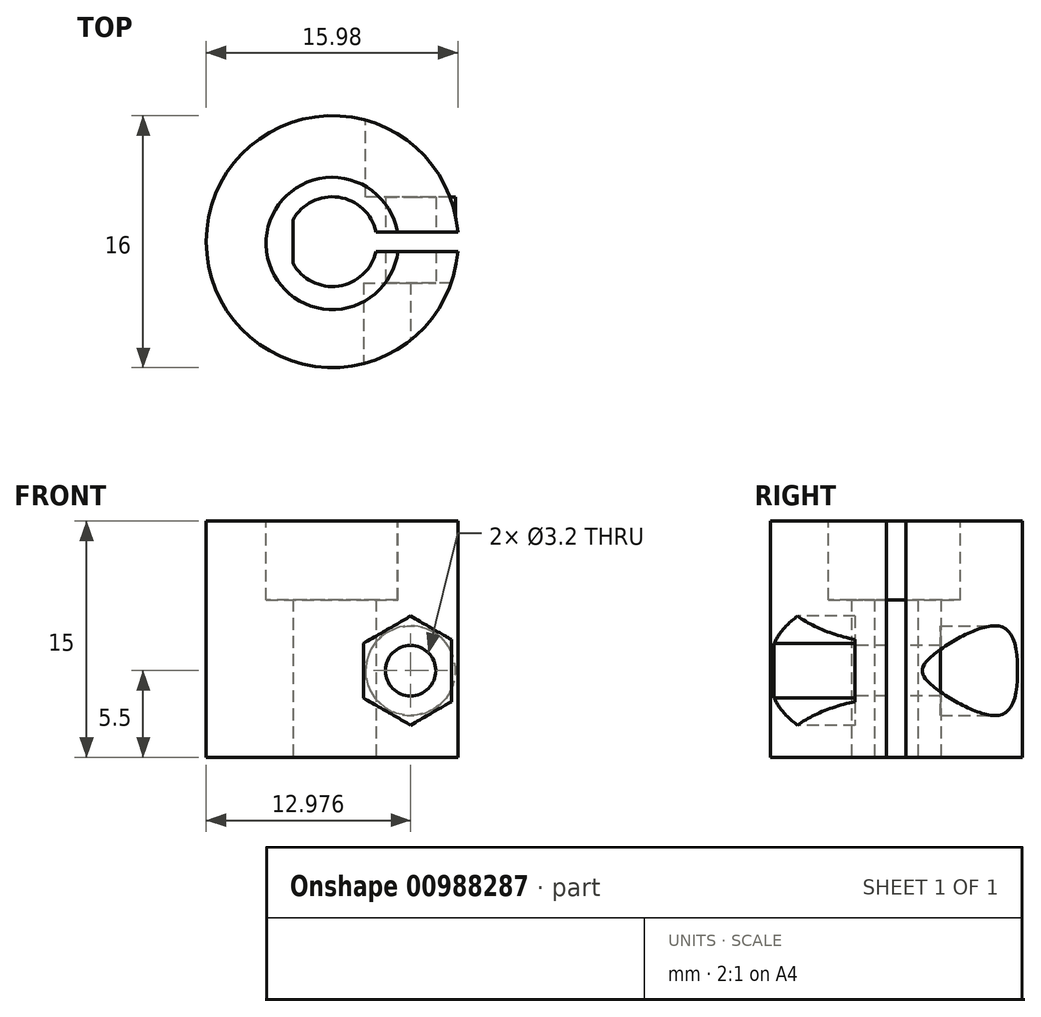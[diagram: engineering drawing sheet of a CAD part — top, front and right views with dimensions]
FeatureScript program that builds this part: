
annotation { "Feature Type Name" : "Feature", "Feature Type Description" : "" }
export const myFeature = defineFeature(function(context is Context, id is Id, definition is map)
    precondition{}
    {
        {
            var Q0;
            Q0=qCreatedBy(makeId("Top.planeOp"),FACE);
            var sketch = newSketch(context, id + "F0", { "sketchPlane" : qUnion([Q0])});
            skCircle(sketch, "E0", {"center": v(0, 0) * mm, "radius": 2.85 * mm});
            skCircle(sketch, "E1", {"center": v(0, 0) * mm, "radius": 8 * mm});
            skLineSegment(sketch, "E2", {"start": v(0, 0) * mm, "end": v(-2.5, 0) * mm});
            skLineSegment(sketch, "E3", {"start": v(-2.5, 0) * mm, "end": v(-2.5, -1.37) * mm});
            skLineSegment(sketch, "E4", {"start": v(-2.5, 0) * mm, "end": v(-2.5, 1.37) * mm});
            skSolve(sketch);
        }
        {
            var Q0;
            Q0=makeQuery(id+"F0.imprint","IMPRINT",FACE,{"disambiguationData":[TD([[makeQuery(id+"F0.imprint","IMPRINT",EDGE,{"derivedFrom":sQuery(id+"F0.wireOp",EDGE,"E0")}),-1.0]])]});
            var Q1;
            {var subQ0=sQuery(id+"F0.wireOp",EDGE,"E3");Q1=makeQuery(id+"F0.imprint","IMPRINT",FACE,{"disambiguationData":[TD([[makeQuery(id+"F0.imprint","IMPRINT",EDGE,{"derivedFrom":subQ0}),-1.0]])]});}
            var Q2;
            {var subQ0=sQuery(id+"F0.wireOp",EDGE,"E3");Q2=makeQuery(id+"F0.imprint","IMPRINT",FACE,{"disambiguationData":[TD([[makeQuery(id+"F0.imprint","IMPRINT",EDGE,{"derivedFrom":subQ0}),1.0]])]});}
            extrude(context, id + "F1", {"entities" : qUnion([Q0, Q1, Q2]), "depth" : 10 * mm, "offsetDistance" : 25 * mm});
        }
        {
            var Q0;
            Q0=makeQuery(id+"F1.opExtrude","CAP_FACE",FACE,{"disambiguationData":[OSD([sQuery(id+"F0.wireOp",EDGE,"E0"),sQuery(id+"F0.wireOp",EDGE,"E1")])],"isStart":false});
            var sketch = newSketch(context, id + "F2", { "sketchPlane" : qUnion([Q0])});
            skCircle(sketch, "E5", {"center": v(0, 0) * mm, "radius": 4.2 * mm});
            skCircle(sketch, "E6", {"center": v(0, 0) * mm, "radius": 8 * mm});
            skSolve(sketch);
        }
        {
            var Q0;
            Q0=makeQuery(id+"F2.imprint","IMPRINT",FACE,{"disambiguationData":[TD([[makeQuery(id+"F2.imprint","IMPRINT",EDGE,{"derivedFrom":sQuery(id+"F2.wireOp",EDGE,"E5")}),-1.0]])]});
            var Q1;
            Q1=makeQuery(id+"F2.imprint","IMPRINT",FACE,{"disambiguationData":[TD([[makeQuery(id+"F2.imprint","IMPRINT",EDGE,{"derivedFrom":sQuery(id+"F2.wireOp",EDGE,"E5")}),1.0]])]});
            extrude(context, id + "F3", {"entities" : qUnion([Q0, Q1]), "operationType" : NewBodyOperationType.ADD, "depth" : 5 * mm, "offsetDistance" : 25 * mm});
        }
        {
            var Q0;
            Q0=makeQuery(id+"F3.opExtrude","CAP_FACE",FACE,{"disambiguationData":[OSD([sQuery(id+"F2.wireOp",EDGE,"E5"),sQuery(id+"F2.wireOp",EDGE,"E6")])],"isStart":false});
            var sketch = newSketch(context, id + "F4", { "sketchPlane" : qUnion([Q0])});
            skLineSegment(sketch, "E7", {"start": v(1.5, 0.62) * mm, "end": v(7.98, 0.62) * mm});
            skLineSegment(sketch, "E8.MirrorCS", {"start": v(1.5, -0.62) * mm, "end": v(7.98, -0.62) * mm});
            skLineSegment(sketch, "E9", {"start": v(1.5, -0.12) * mm, "end": v(1.5, -0.62) * mm});
            skLineSegment(sketch, "E10", {"start": v(1.5, 0.62) * mm, "end": v(1.5, -0.12) * mm});
            skCircle(sketch, "E11", {"center": v(0, -0.12) * mm, "radius": 4.2 * mm});
            skSolve(sketch);
        }
        {
            var Q0;
            {var subQ5=sQuery(id+"F4.wireOp",EDGE,"3cT3lrrN-qn0D-v2Yr-26uK-GXx553Q63k6q");Q0=makeQuery(id+"F4.imprint","IMPRINT",FACE,{"disambiguationData":[TD([[makeQuery(id+"F4.imprint","IMPRINT",EDGE,{"derivedFrom":subQ5}),-1.0]])]});}
            var Q1;
            {var subQ0=sQuery(id+"F4.wireOp",EDGE,"E7");var subQ1=makeQuery(id+"F3.opExtrude","CAP_EDGE",EDGE,{"disambiguationData":[OSD([sQuery(id+"F2.wireOp",EDGE,"E6")])],"isStart":false});var subQ2=makeQuery(id+"F4.imprint","INTERSECT",VERTEX,{"derivedFrom":[subQ1,subQ0]});Q1=makeQuery(id+"F4.imprint","IMPRINT",FACE,{"disambiguationData":[TD([[makeQuery(id+"F4.imprint","IMPRINT",EDGE,{"disambiguationData":[TD([[subQ2,1.0]])],"derivedFrom":subQ0}),-1.0]])]});}
            var Q2;
            {var subQ0=sQuery(id+"F4.wireOp",EDGE,"h4iLg6Yi-2gNe-oge3-7Yi7-5BReb18L3EgM");var subQ1=sQuery(id+"F4.wireOp",EDGE,"E7");var subQ2=makeQuery(id+"F4.imprint","INTERSECT",VERTEX,{"derivedFrom":[subQ1,subQ0]});Q2=makeQuery(id+"F4.imprint","IMPRINT",FACE,{"disambiguationData":[TD([[makeQuery(id+"F4.imprint","IMPRINT",EDGE,{"disambiguationData":[TD([[subQ2,1.0]])],"derivedFrom":subQ1}),-1.0]])]});}
            var Q3;
            {var subQ0=sQuery(id+"F4.wireOp",EDGE,"E10");Q3=makeQuery(id+"F4.imprint","IMPRINT",FACE,{"disambiguationData":[TD([[makeQuery(id+"F4.imprint","IMPRINT",EDGE,{"derivedFrom":subQ0}),1.0]])]});}
            extrude(context, id + "F5", {"entities" : qUnion([Q0, Q1, Q2, Q3]), "operationType" : NewBodyOperationType.REMOVE, "oppositeDirection" : true, "depth" : 25 * mm, "offsetDistance" : 25 * mm});
        }
        {
            var Q0;
            Q0=makeQuery(id+"F5.boolean.opBoolean","COPY",FACE,{"derivedFrom":makeQuery(id+"F5.opExtrude","SWEPT_FACE",FACE,{"disambiguationData":[OSD([sQuery(id+"F4.wireOp",EDGE,"E7")])]})});
            var sketch = newSketch(context, id + "F6", { "sketchPlane" : qUnion([Q0])});
            skLineSegment(sketch, "E12", {"start": v(7.98, 7.5) * mm, "end": v(4.98, 7.5) * mm});
            skPoint(sketch, "E12.endSnap0", {"position": v(7.98, 7.5) * mm});
            skLineSegment(sketch, "E13", {"start": v(4.98, 7.5) * mm, "end": v(4.98, 5.5) * mm});
            skCircle(sketch, "E14", {"center": v(4.98, 5.5) * mm, "radius": 1.6 * mm});
            skCircle(sketch, "E15", {"center": v(4.98, 5.5) * mm, "radius": 2.85 * mm});
            skPoint(sketch, "E16.startSnap0", {"position": v(4.74, 0) * mm});
            skPoint(sketch, "E17.startSnap0", {"position": v(2.45, 3) * mm});
            skSolve(sketch);
        }
        {
            var Q0;
            Q0=makeQuery(id+"F5.boolean.opBoolean","COPY",FACE,{"derivedFrom":makeQuery(id+"F5.opExtrude","SWEPT_FACE",FACE,{"disambiguationData":[OSD([sQuery(id+"F4.wireOp",EDGE,"E8.MirrorCS")])]})});
            var sketch = newSketch(context, id + "F7", { "sketchPlane" : qUnion([Q0])});
            skLineSegment(sketch, "E18", {"start": v(-7.98, 7.5) * mm, "end": v(-4.98, 7.5) * mm});
            skLineSegment(sketch, "E19", {"start": v(-4.98, 7.5) * mm, "end": v(-4.98, 5.5) * mm});
            skCircle(sketch, "E20", {"center": v(-4.98, 5.5) * mm, "radius": 1.6 * mm});
            skCircle(sketch, "E21", {"center": v(-4.98, 5.5) * mm, "radius": 2.25 * mm});
            skSolve(sketch);
        }
        {
            var Q0;
            {var subQ0=sQuery(id+"F6.wireOp",EDGE,"E15");var subQ1=makeQuery(id+"F5.opExtrude","SWEPT_FACE",FACE,{"disambiguationData":[OSD([sQuery(id+"F4.wireOp",EDGE,"E7")])]});var subQ2=makeQuery(id+"F5.boolean.opBoolean","INTERSECT",EDGE,{"derivedFrom":[makeQuery(id+"F3.opExtrude","SWEPT_FACE",FACE,{"disambiguationData":[OSD([sQuery(id+"F2.wireOp",EDGE,"E5")])]}),subQ1]});var subQ3=makeQuery(id+"F6.imprint","INTERSECT",VERTEX,{"derivedFrom":[subQ2,subQ0]});Q0=makeQuery(id+"F6.imprint","IMPRINT",FACE,{"disambiguationData":[TD([[makeQuery(id+"F6.imprint","IMPRINT",EDGE,{"disambiguationData":[TD([[subQ3,-1.0]])],"derivedFrom":subQ0}),1.0]])]});}
            var Q1;
            Q1=makeQuery(id+"F6.imprint","IMPRINT",FACE,{"disambiguationData":[TD([[makeQuery(id+"F6.imprint","IMPRINT",EDGE,{"derivedFrom":sQuery(id+"F6.wireOp",EDGE,"E14")}),-1.0]])]});
            var Q2;
            {var subQ0=sQuery(id+"F6.wireOp",EDGE,"E15");var subQ1=makeQuery(id+"F5.boolean.opBoolean","INTERSECT",EDGE,{"derivedFrom":[makeQuery(id+"F1.opExtrude","SWEPT_FACE",FACE,{"disambiguationData":[OSD([sQuery(id+"F0.wireOp",EDGE,"E0")])]}),makeQuery(id+"F5.opExtrude","SWEPT_FACE",FACE,{"disambiguationData":[OSD([sQuery(id+"F4.wireOp",EDGE,"E7")])]})]});var subQ2=makeQuery(id+"F6.imprint","INTERSECT",VERTEX,{"disambiguationData":[OD(0.0)],"derivedFrom":[subQ1,subQ0]});Q2=makeQuery(id+"F6.imprint","IMPRINT",FACE,{"disambiguationData":[TD([[makeQuery(id+"F6.imprint","IMPRINT",EDGE,{"disambiguationData":[TD([[subQ2,-1.0]])],"derivedFrom":subQ0}),1.0]])]});}
            var Q3;
            {var subQ8=sQuery(id+"F6.wireOp",EDGE,"2gh9ahhL-McAf-w0sG-yJkm-cRXL0FyeZt4c");Q3=makeQuery(id+"F6.imprint","IMPRINT",FACE,{"disambiguationData":[TD([[makeQuery(id+"F6.imprint","IMPRINT",EDGE,{"derivedFrom":subQ8}),1.0]])]});}
            var Q4;
            {var subQ0=sQuery(id+"F6.wireOp",EDGE,"uBxah9m0-Ykx7-MwLP-dEoF-epf6zd2HYMo8");Q4=makeQuery(id+"F6.imprint","IMPRINT",FACE,{"disambiguationData":[TD([[makeQuery(id+"F6.imprint","IMPRINT",EDGE,{"derivedFrom":subQ0}),1.0]])]});}
            var Q5;
            {var subQ1=sQuery(id+"F6.wireOp",EDGE,"E12");var subQ6=sQuery(id+"F6.wireOp",EDGE,"E13");var subQ9=makeQuery(id+"F6.imprint","INTERSECT",VERTEX,{"derivedFrom":[subQ1,subQ6]});Q5=makeQuery(id+"F6.imprint","IMPRINT",FACE,{"disambiguationData":[TD([[makeQuery(id+"F6.imprint","IMPRINT",EDGE,{"disambiguationData":[TD([[subQ9,1.0]])],"derivedFrom":subQ1}),1.0]])]});}
            var Q6;
            {var subQ1=sQuery(id+"F6.wireOp",EDGE,"E13");var subQ5=sQuery(id+"F6.wireOp",EDGE,"E12");var subQ6=makeQuery(id+"F6.imprint","INTERSECT",VERTEX,{"derivedFrom":[subQ5,subQ1]});Q6=makeQuery(id+"F6.imprint","IMPRINT",FACE,{"disambiguationData":[TD([[makeQuery(id+"F6.imprint","IMPRINT",EDGE,{"disambiguationData":[TD([[subQ6,1.0]])],"derivedFrom":subQ5}),-1.0]])]});}
            extrude(context, id + "F8", {"entities" : qUnion([Q0, Q1, Q2, Q3, Q4, Q5, Q6]), "operationType" : NewBodyOperationType.ADD, "oppositeDirection" : true, "depth" : 8.7 * mm, "offsetDistance" : 25 * mm});
        }
        {
            var Q0;
            Q0=makeQuery(id+"F8.opExtrude","CAP_FACE",FACE,{"disambiguationData":[OSD([sQuery(id+"F6.wireOp",EDGE,"E14"),sQuery(id+"F6.wireOp",EDGE,"E15")])],"isStart":false});
            extrude(context, id + "F9", {"entities" : qUnion([Q0]), "operationType" : NewBodyOperationType.REMOVE, "oppositeDirection" : true, "depth" : 6.5 * mm, "offsetDistance" : 25 * mm});
        }
        {
            var Q0;
            Q0=makeQuery(id+"F7.imprint","IMPRINT",FACE,{"disambiguationData":[TD([[makeQuery(id+"F7.imprint","IMPRINT",EDGE,{"derivedFrom":sQuery(id+"F7.wireOp",EDGE,"E20")}),-1.0]])]});
            var Q1;
            {var subQ0=sQuery(id+"F7.wireOp",EDGE,"oPrDCR9T-XhIv-hLaT-Qq2s-SmJo2KBhPsKR");var subQ1=makeQuery(id+"F5.boolean.opBoolean","COPY",EDGE,{"derivedFrom":makeQuery(id+"F5.opExtrude","SWEPT_EDGE",EDGE,{"disambiguationData":[OSD([sQuery(id+"F0.wireOp",EDGE,"E0"),sQuery(id+"F4.wireOp",EDGE,"E8.MirrorCS")])]})});var subQ2=makeQuery(id+"F7.imprint","INTERSECT",VERTEX,{"disambiguationData":[OD(0.0)],"derivedFrom":[subQ1,subQ0]});Q1=makeQuery(id+"F7.imprint","IMPRINT",FACE,{"disambiguationData":[TD([[makeQuery(id+"F7.imprint","IMPRINT",EDGE,{"disambiguationData":[TD([[subQ2,1.0]])],"derivedFrom":subQ0}),1.0]])]});}
            extrude(context, id + "F10", {"entities" : qUnion([Q0, Q1]), "operationType" : NewBodyOperationType.ADD, "oppositeDirection" : true, "depth" : 10 * mm, "offsetDistance" : 25 * mm});
        }
        {
            var Q0;
            Q0=makeQuery(id+"F10.opExtrude","CAP_FACE",FACE,{"disambiguationData":[OSD([sQuery(id+"F7.wireOp",EDGE,"E20"),sQuery(id+"F7.wireOp",EDGE,"oPrDCR9T-XhIv-hLaT-Qq2s-SmJo2KBhPsKR")])],"isStart":false});
            var sketch = newSketch(context, id + "F11", { "sketchPlane" : qUnion([Q0])});
            skLineSegment(sketch, "E22", {"start": v(0, 0) * mm, "end": v(8, 0) * mm});
            skLineSegment(sketch, "E23", {"start": v(8, 0) * mm, "end": v(8, 3) * mm});
            skLineSegment(sketch, "E24", {"start": v(8, 3) * mm, "end": v(4.98, 5.5) * mm});
            skCircle(sketch, "E25", {"center": v(4.98, 5.5) * mm, "radius": 1.65 * mm});
            skCircle(sketch, "E26.cCircle", {"center": v(4.98, 5.5) * mm, "radius": 3 * mm, "construction": true});
            skLineSegment(sketch, "E26.0", {"start": v(7.98, 7.23) * mm, "end": v(7.98, 3.77) * mm});
            skLineSegment(sketch, "E26.1", {"start": v(7.98, 3.77) * mm, "end": v(4.98, 2.04) * mm});
            skLineSegment(sketch, "E26.2", {"start": v(4.98, 2.04) * mm, "end": v(1.98, 3.77) * mm});
            skLineSegment(sketch, "E26.3", {"start": v(1.98, 3.77) * mm, "end": v(1.98, 7.23) * mm});
            skLineSegment(sketch, "E26.4", {"start": v(1.98, 7.23) * mm, "end": v(4.98, 8.96) * mm});
            skLineSegment(sketch, "E26.5", {"start": v(4.98, 8.96) * mm, "end": v(7.98, 7.23) * mm});
            skPoint(sketch, "E26.0.midPoint", {"position": v(7.98, 5.5) * mm});
            skSolve(sketch);
        }
        {
            var Q0;
            {var subQ4=sQuery(id+"F11.wireOp",EDGE,"E23");Q0=makeQuery(id+"F11.imprint","IMPRINT",FACE,{"disambiguationData":[TD([[makeQuery(id+"F11.imprint","IMPRINT",EDGE,{"derivedFrom":subQ4}),1.0]])]});}
            var Q1;
            Q1=makeQuery(id+"F11.imprint","IMPRINT",FACE,{"disambiguationData":[TD([[makeQuery(id+"F11.imprint","IMPRINT",EDGE,{"derivedFrom":makeQuery(id+"F10.opExtrude","CAP_EDGE",EDGE,{"disambiguationData":[OSD([sQuery(id+"F7.wireOp",EDGE,"E20")])],"isStart":false})}),-1.0]])]});
            var Q2;
            Q2=makeQuery(id+"F11.imprint","IMPRINT",FACE,{"disambiguationData":[TD([[makeQuery(id+"F11.imprint","IMPRINT",EDGE,{"derivedFrom":sQuery(id+"F11.wireOp",EDGE,"32d43d9b-7006-4c65-a779-6c69e89be51d.0")}),-1.0]])]});
            var Q3;
            Q3=makeQuery(id+"F11.imprint","IMPRINT",FACE,{"disambiguationData":[TD([[makeQuery(id+"F11.imprint","IMPRINT",EDGE,{"derivedFrom":makeQuery(id+"F10.opExtrude","CAP_EDGE",EDGE,{"disambiguationData":[OSD([sQuery(id+"F7.wireOp",EDGE,"E20")])],"isStart":false})}),1.0]])]});
            var Q4;
            {var subQ1=sQuery(id+"F7.wireOp",EDGE,"E21");var subQ10=makeQuery(id+"F10.opExtrude","CAP_EDGE",EDGE,{"disambiguationData":[OSD([subQ1])],"isStart":false});Q4=makeQuery(id+"F11.imprint","IMPRINT",FACE,{"disambiguationData":[TD([[makeQuery(id+"F11.imprint","IMPRINT",EDGE,{"derivedFrom":subQ10}),-1.0]])]});}
            var Q5;
            {var subQ2=sQuery(id+"F11.wireOp",EDGE,"E26.0");Q5=makeQuery(id+"F11.imprint","IMPRINT",FACE,{"disambiguationData":[TD([[makeQuery(id+"F11.imprint","IMPRINT",EDGE,{"derivedFrom":subQ2}),-1.0]])]});}
            extrude(context, id + "F12", {"entities" : qUnion([Q0, Q1, Q2, Q3, Q4, Q5]), "operationType" : NewBodyOperationType.REMOVE, "oppositeDirection" : true, "depth" : 8 * mm, "offsetDistance" : 25 * mm});
        }
        {
            var Q0;
            {var subQ0=sQuery(id+"F4.wireOp",EDGE,"E10");Q0=makeQuery(id+"F4.imprint","IMPRINT",FACE,{"disambiguationData":[TD([[makeQuery(id+"F4.imprint","IMPRINT",EDGE,{"derivedFrom":subQ0}),-1.0]])]});}
            var Q1;
            {var subQ0=sQuery(id+"F4.wireOp",EDGE,"E10");Q1=makeQuery(id+"F4.imprint","IMPRINT",FACE,{"disambiguationData":[TD([[makeQuery(id+"F4.imprint","IMPRINT",EDGE,{"derivedFrom":subQ0}),1.0]])]});}
            extrude(context, id + "F13", {"entities" : qUnion([Q0, Q1]), "operationType" : NewBodyOperationType.REMOVE, "oppositeDirection" : true, "depth" : 5 * mm, "offsetDistance" : 25 * mm});
        }
        {
            var Q0;
            {var subQ0=sQuery(id+"F0.wireOp",EDGE,"E3");Q0=makeQuery(id+"F0.imprint","IMPRINT",FACE,{"disambiguationData":[TD([[makeQuery(id+"F0.imprint","IMPRINT",EDGE,{"derivedFrom":subQ0}),1.0]])]});}
            extrude(context, id + "F14", {"entities" : qUnion([Q0]), "operationType" : NewBodyOperationType.REMOVE, "depth" : 10 * mm, "offsetDistance" : 25 * mm});
        }
        {
            var Q0;
            {var subQ4=sQuery(id+"F7.wireOp",EDGE,"E20");var subQ6=makeQuery(id+"F10.opExtrude","CAP_EDGE",EDGE,{"disambiguationData":[OSD([subQ4])],"isStart":false});Q0=makeQuery(id+"F11.imprint","IMPRINT",FACE,{"disambiguationData":[TD([[makeQuery(id+"F11.imprint","IMPRINT",EDGE,{"derivedFrom":subQ6}),-1.0]])]});}
            extrude(context, id + "F15", {"entities" : qUnion([Q0]), "operationType" : NewBodyOperationType.REMOVE, "oppositeDirection" : true, "depth" : 25 * mm, "offsetDistance" : 25 * mm});
        }
    });
